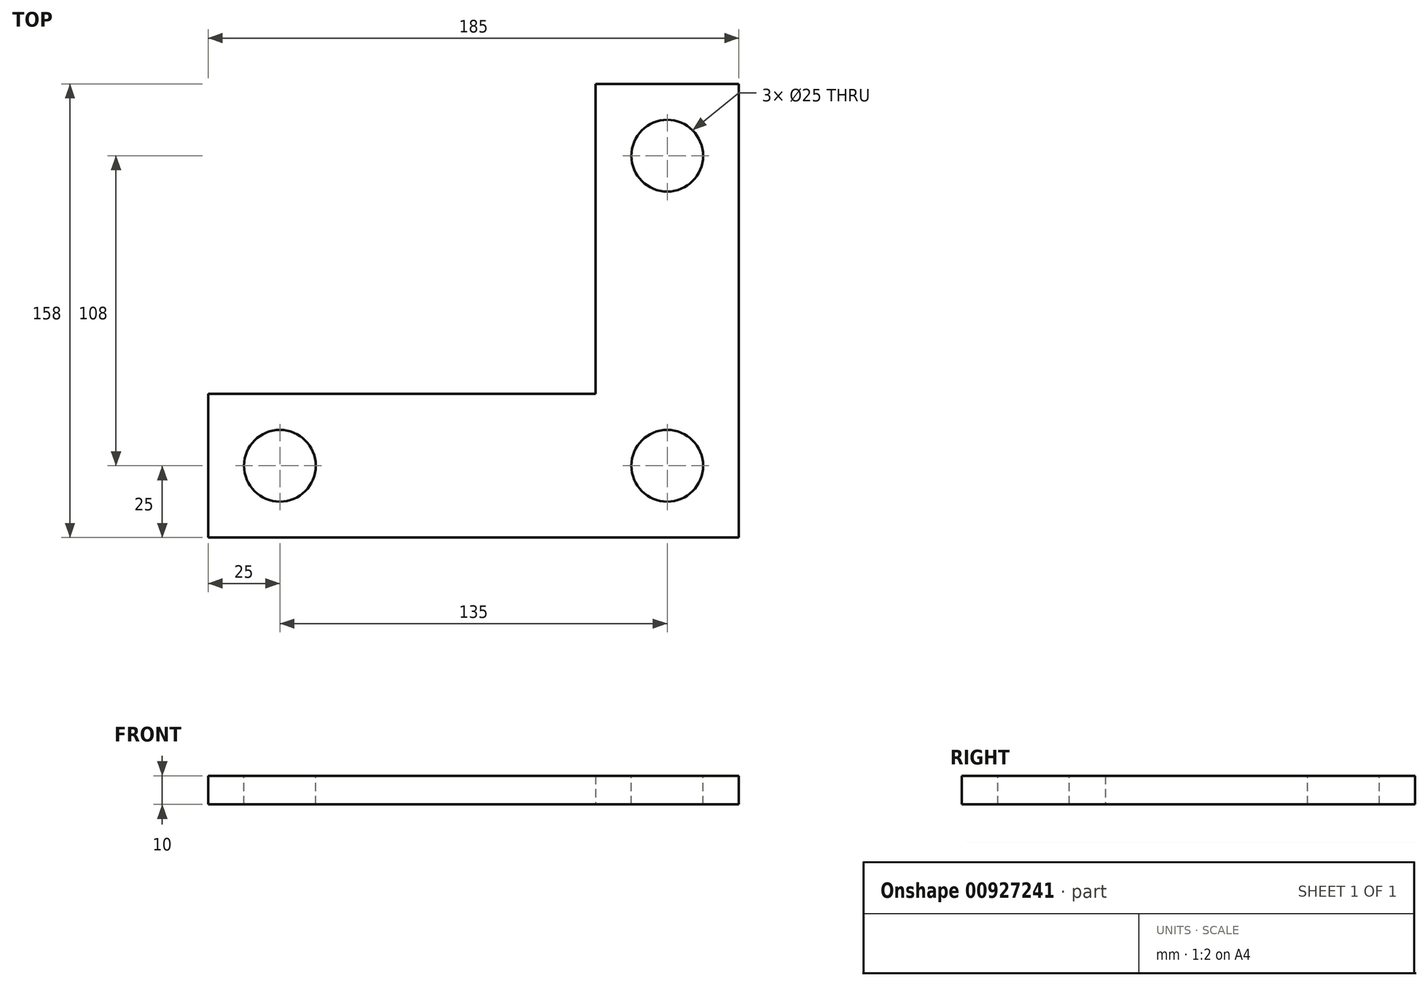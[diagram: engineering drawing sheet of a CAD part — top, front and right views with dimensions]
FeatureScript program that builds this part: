
annotation { "Feature Type Name" : "Feature", "Feature Type Description" : "" }
export const myFeature = defineFeature(function(context is Context, id is Id, definition is map)
    precondition{}
    {
        {
            var Q0;
            Q0=qCreatedBy(makeId("Top.planeOp"),FACE);
            var sketch = newSketch(context, id + "F0", { "sketchPlane" : qUnion([Q0])});
            skLineSegment(sketch, "E0.bottom", {"start": v(42.5, 25) * mm, "end": v(-92.5, 25) * mm});
            skLineSegment(sketch, "E0.top", {"start": v(92.5, -25) * mm, "end": v(-92.5, -25) * mm});
            skLineSegment(sketch, "E0.left", {"start": v(92.5, 133) * mm, "end": v(92.5, -25) * mm});
            skLineSegment(sketch, "E0.right", {"start": v(-92.5, 25) * mm, "end": v(-92.5, -25) * mm});
            skPoint(sketch, "E0.middle", {"position": v(0, 0) * mm});
            skLineSegment(sketch, "E1", {"start": v(92.5, 133) * mm, "end": v(42.5, 133) * mm});
            skLineSegment(sketch, "E2", {"start": v(42.5, 133) * mm, "end": v(42.5, 25) * mm});
            skPoint(sketch, "E3.orphan", {"position": v(92.5, 25) * mm});
            skSolve(sketch);
        }
        {
            var Q0;
            Q0=makeQuery(id+"F0.imprint","IMPRINT",FACE,{"disambiguationData":[TD([[makeQuery(id+"F0.imprint","IMPRINT",EDGE,{"derivedFrom":sQuery(id+"F0.wireOp",EDGE,"E0.bottom")}),1.0]])]});
            extrude(context, id + "F1", {"entities" : qUnion([Q0]), "depth" : 10 * mm, "offsetDistance" : 25 * mm});
        }
        {
            var Q0;
            Q0=makeQuery(id+"F1.opExtrude","CAP_FACE",FACE,{"disambiguationData":[OSD([sQuery(id+"F0.wireOp",EDGE,"E0.bottom"),sQuery(id+"F0.wireOp",EDGE,"E0.top"),sQuery(id+"F0.wireOp",EDGE,"E0.left"),sQuery(id+"F0.wireOp",EDGE,"E0.right")])],"isStart":false});
            var sketch = newSketch(context, id + "F2", { "sketchPlane" : qUnion([Q0])});
            skLineSegment(sketch, "E4", {"start": v(-67.5, 0) * mm, "end": v(67.5, 0) * mm});
            skLineSegment(sketch, "E5", {"start": v(67.5, 0) * mm, "end": v(67.5, 108) * mm});
            skSolve(sketch);
        }
        {
            var Q0;
            Q0=sQuery(id+"F2.wireOp",VERTEX,"E4.start");
            var Q1;
            Q1=sQuery(id+"F2.wireOp",VERTEX,"E4.end");
            var Q2;
            Q2=sQuery(id+"F2.wireOp",VERTEX,"E5.end");
            var Q3;
            Q3=makeQuery(id+"F1.opExtrude","SWEPT_BODY",BODY,{"disambiguationData":[OSD([sQuery(id+"F0.wireOp",EDGE,"E0.bottom"),sQuery(id+"F0.wireOp",EDGE,"E0.top"),sQuery(id+"F0.wireOp",EDGE,"E0.left"),sQuery(id+"F0.wireOp",EDGE,"E0.right")])]});
            hole(context, id + "F3", {"style" : HoleStyle.SIMPLE, "endStyle" : HoleEndStyle.THROUGH, "holeDiameter" : 25 * mm, "majorDiameter" : 5 * mm, "isTappedThrough" : true, "tappedDepth" : 12 * mm, "tapClearance" : 3, "locations" : qUnion([Q0, Q1, Q2]), "scope" : qUnion([Q3])});
        }
    });
